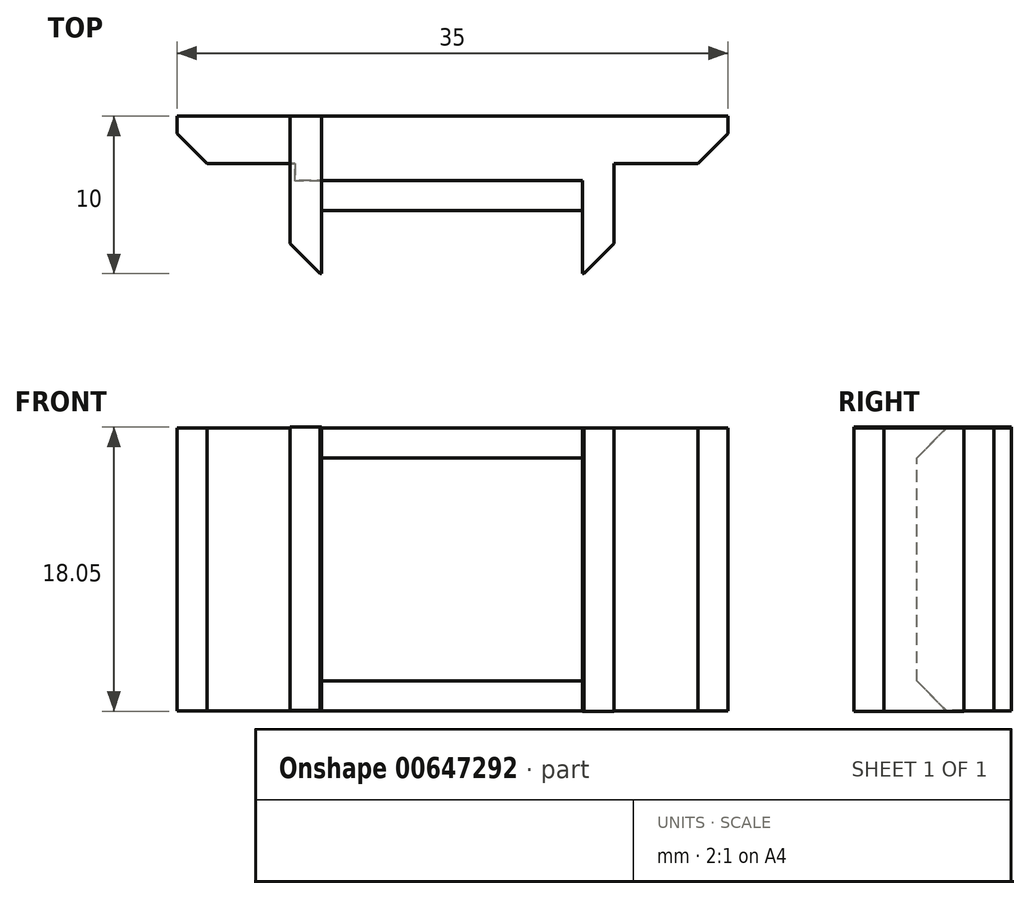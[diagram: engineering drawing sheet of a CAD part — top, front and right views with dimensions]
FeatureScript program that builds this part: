
annotation { "Feature Type Name" : "Feature", "Feature Type Description" : "" }
export const myFeature = defineFeature(function(context is Context, id is Id, definition is map)
    precondition{}
    {
        {
            var Q0;
            Q0=qCreatedBy(makeId("Front.planeOp"),FACE);
            var sketch = newSketch(context, id + "F0", { "sketchPlane" : qUnion([Q0])});
            skLineSegment(sketch, "E0.bottom", {"start": v(10, 9) * mm, "end": v(-10, 9) * mm});
            skLineSegment(sketch, "E0.top", {"start": v(10, -9) * mm, "end": v(-10, -9) * mm});
            skLineSegment(sketch, "E0.left", {"start": v(10, 9) * mm, "end": v(10, -9) * mm});
            skLineSegment(sketch, "E0.right", {"start": v(-10, 9) * mm, "end": v(-10, -9) * mm});
            skPoint(sketch, "E0.middle", {"position": v(0, 0) * mm});
            skSolve(sketch);
        }
        {
            var Q0;
            Q0=makeQuery(id+"F0.imprint","IMPRINT",FACE,{"disambiguationData":[TD([[makeQuery(id+"F0.imprint","IMPRINT",EDGE,{"derivedFrom":sQuery(id+"F0.wireOp",EDGE,"E0.bottom")}),1.0]])]});
            extrude(context, id + "F1", {"entities" : qUnion([Q0]), "depth" : 6 * mm, "offsetDistance" : 25.4 * mm});
        }
        {
            var Q0;
            Q0=qCreatedBy(makeId("Front.planeOp"),FACE);
            var sketch = newSketch(context, id + "F2", { "sketchPlane" : qUnion([Q0])});
            skLineSegment(sketch, "E1.bottom", {"start": v(-10.32, 9.04) * mm, "end": v(-8.32, 9.04) * mm});
            skLineSegment(sketch, "E1.top", {"start": v(-10.32, -8.96) * mm, "end": v(-8.32, -8.96) * mm});
            skLineSegment(sketch, "E1.left", {"start": v(-10.32, 9.04) * mm, "end": v(-10.32, -8.96) * mm});
            skLineSegment(sketch, "E1.right", {"start": v(-8.32, 9.04) * mm, "end": v(-8.32, -8.96) * mm});
            skLineSegment(sketch, "E2.bottom", {"start": v(10.27, 9) * mm, "end": v(8.27, 9) * mm});
            skLineSegment(sketch, "E2.top", {"start": v(10.27, -9) * mm, "end": v(8.27, -9) * mm});
            skLineSegment(sketch, "E2.left", {"start": v(10.27, 9) * mm, "end": v(10.27, -9) * mm});
            skLineSegment(sketch, "E2.right", {"start": v(8.27, 9) * mm, "end": v(8.27, -9) * mm});
            skSolve(sketch);
        }
        {
            var Q0;
            Q0=makeQuery(id+"F2.imprint","IMPRINT",FACE,{"disambiguationData":[TD([[makeQuery(id+"F2.imprint","IMPRINT",EDGE,{"derivedFrom":sQuery(id+"F2.wireOp",EDGE,"E2.bottom")}),1.0]])]});
            var Q1;
            Q1=makeQuery(id+"F2.imprint","IMPRINT",FACE,{"disambiguationData":[TD([[makeQuery(id+"F2.imprint","IMPRINT",EDGE,{"derivedFrom":sQuery(id+"F2.wireOp",EDGE,"E1.bottom")}),-1.0]])]});
            extrude(context, id + "F3", {"entities" : qUnion([Q0, Q1]), "operationType" : NewBodyOperationType.ADD, "depth" : 10 * mm, "offsetDistance" : 25.4 * mm});
        }
        {
            var Q0;
            Q0=qCreatedBy(makeId("Front.planeOp"),FACE);
            var sketch = newSketch(context, id + "F4", { "sketchPlane" : qUnion([Q0])});
            skLineSegment(sketch, "E3.bottom", {"start": v(17.5, 9) * mm, "end": v(-17.5, 9) * mm});
            skLineSegment(sketch, "E3.top", {"start": v(17.5, -9) * mm, "end": v(-17.5, -9) * mm});
            skLineSegment(sketch, "E3.left", {"start": v(17.5, 9) * mm, "end": v(17.5, -9) * mm});
            skLineSegment(sketch, "E3.right", {"start": v(-17.5, 9) * mm, "end": v(-17.5, -9) * mm});
            skPoint(sketch, "E3.middle", {"position": v(0, 0) * mm});
            skSolve(sketch);
        }
        {
            var Q0;
            Q0=makeQuery(id+"F4.imprint","IMPRINT",FACE,{"disambiguationData":[TD([[makeQuery(id+"F4.imprint","IMPRINT",EDGE,{"derivedFrom":sQuery(id+"F4.wireOp",EDGE,"E3.bottom")}),1.0]])]});
            extrude(context, id + "F5", {"entities" : qUnion([Q0]), "operationType" : NewBodyOperationType.ADD, "depth" : 3 * mm, "offsetDistance" : 25.4 * mm});
        }
        {
            var Q0;
            Q0=makeQuery(id+"F5.opExtrude","CAP_EDGE",EDGE,{"disambiguationData":[OSD([sQuery(id+"F4.wireOp",EDGE,"E3.right")])],"isStart":false});
            var Q1;
            Q1=makeQuery(id+"F5.opExtrude","CAP_EDGE",EDGE,{"disambiguationData":[OSD([sQuery(id+"F4.wireOp",EDGE,"E3.left")])],"isStart":false});
            var Q2;
            Q2=makeQuery(id+"F3.opExtrude","CAP_EDGE",EDGE,{"disambiguationData":[OSD([sQuery(id+"F2.wireOp",EDGE,"E2.left")])],"isStart":false});
            var Q3;
            Q3=makeQuery(id+"F3.opExtrude","CAP_EDGE",EDGE,{"disambiguationData":[OSD([sQuery(id+"F2.wireOp",EDGE,"E1.left")])],"isStart":false});
            var Q4;
            Q4=makeQuery(id+"F1.opExtrude","CAP_EDGE",EDGE,{"disambiguationData":[OSD([sQuery(id+"F0.wireOp",EDGE,"E0.bottom")])],"isStart":false});
            var Q5;
            Q5=makeQuery(id+"F1.opExtrude","CAP_EDGE",EDGE,{"disambiguationData":[OSD([sQuery(id+"F0.wireOp",EDGE,"E0.top")])],"isStart":false});
            chamfer(context, id + "F6", {"entities" : qUnion([Q0, Q1, Q2, Q3, Q4, Q5]), "width" : 1.9 * mm, "tangentPropagation" : true});
        }
    });
